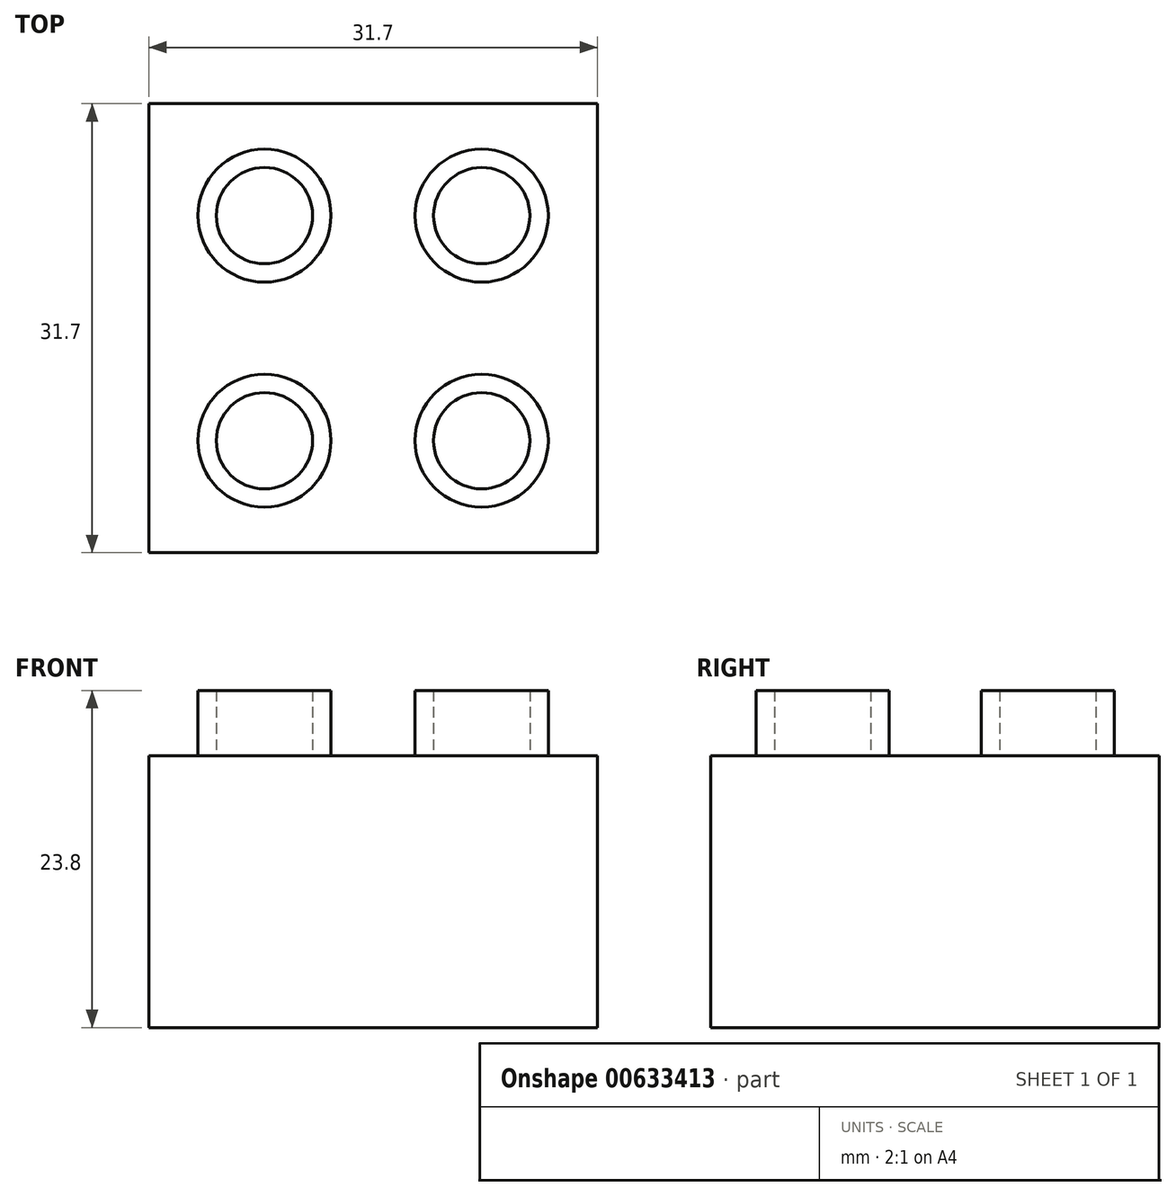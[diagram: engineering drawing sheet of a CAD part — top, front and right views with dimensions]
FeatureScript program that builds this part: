
annotation { "Feature Type Name" : "Feature", "Feature Type Description" : "" }
export const myFeature = defineFeature(function(context is Context, id is Id, definition is map)
    precondition{}
    {
        {
            var Q0;
            Q0=qCreatedBy(makeId("Top.planeOp"),FACE);
            var sketch = newSketch(context, id + "F0", { "sketchPlane" : qUnion([Q0])});
            skLineSegment(sketch, "E0.bottom", {"start": v(-15.85, 15.85) * mm, "end": v(15.85, 15.85) * mm});
            skLineSegment(sketch, "E0.top", {"start": v(-15.85, -15.85) * mm, "end": v(15.85, -15.85) * mm});
            skLineSegment(sketch, "E0.left", {"start": v(-15.85, 15.85) * mm, "end": v(-15.85, -15.85) * mm});
            skLineSegment(sketch, "E0.right", {"start": v(15.85, 15.85) * mm, "end": v(15.85, -15.85) * mm});
            skSolve(sketch);
        }
        {
            var Q0;
            Q0 = qSketchRegion(id + "F0", true);
            extrude(context, id + "F1", {"entities" : qUnion([Q0]), "depth" : 19.2 * mm, "offsetDistance" : 25 * mm});
        }
        {
            var Q0;
            Q0=makeQuery(id+"F1.opExtrude","CAP_FACE",FACE,{"disambiguationData":[OSD([sQuery(id+"F0.wireOp",EDGE,"E0.bottom"),sQuery(id+"F0.wireOp",EDGE,"E0.top"),sQuery(id+"F0.wireOp",EDGE,"E0.left"),sQuery(id+"F0.wireOp",EDGE,"E0.right")])],"isStart":false});
            var sketch = newSketch(context, id + "F2", { "sketchPlane" : qUnion([Q0])});
            skLineSegment(sketch, "E1", {"start": v(-20.78, 7.95) * mm, "end": v(23.42, 7.95) * mm, "construction": true});
            skCircle(sketch, "E2", {"center": v(-7.67, 7.95) * mm, "radius": 3.4 * mm});
            skCircle(sketch, "E3", {"center": v(-7.67, 7.95) * mm, "radius": 4.7 * mm});
            skCircle(sketch, "E4.MirrorC", {"center": v(7.67, 7.95) * mm, "radius": 3.4 * mm});
            skCircle(sketch, "E5.MirrorC", {"center": v(7.67, 7.95) * mm, "radius": 4.7 * mm});
            skCircle(sketch, "E6.MirrorC", {"center": v(-7.67, -7.95) * mm, "radius": 4.7 * mm});
            skCircle(sketch, "E7.MirrorC", {"center": v(7.67, -7.95) * mm, "radius": 4.7 * mm});
            skCircle(sketch, "E8.MirrorC", {"center": v(-7.67, -7.95) * mm, "radius": 3.4 * mm});
            skCircle(sketch, "E9.MirrorC", {"center": v(7.67, -7.95) * mm, "radius": 3.4 * mm});
            skSolve(sketch);
        }
        {
            var Q0;
            Q0 = qSketchRegion(id + "F2", true);
            extrude(context, id + "F3", {"entities" : qUnion([Q0]), "operationType" : NewBodyOperationType.ADD, "depth" : 4.6 * mm, "offsetDistance" : 25 * mm});
        }
    });
